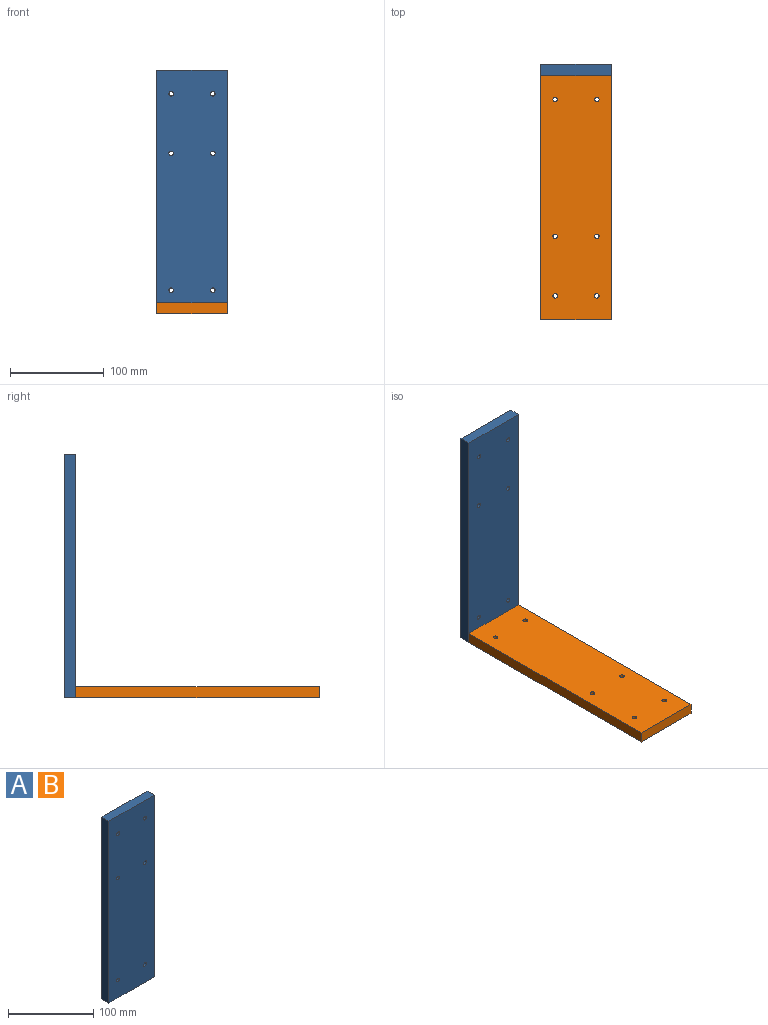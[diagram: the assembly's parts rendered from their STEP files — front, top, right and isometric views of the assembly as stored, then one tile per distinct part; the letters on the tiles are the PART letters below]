
ASSEMBLY  parts=2 mates=1
PART A: 12 faces, bbox 75x11.8x260.4 mm
  f0: plane 260.35x11.75mm, normal (1,0,0), area 3059.1mm2, adj f1,f3,f4,f5
  f1: plane 75x11.75mm, normal (0,0,1), area 881.2mm2, adj f0,f2,f4,f5
  f2: plane 260.35x11.75mm, normal (-1,0,0), area 3059.1mm2, adj f1,f3,f4,f5
  f3: plane 75x11.75mm, normal (0,0,-1), area 881.2mm2, adj f0,f2,f4,f5
  f4: plane 260.35x75mm, normal (0,-1,0), area 19419.4mm2, adj f0,f1,f2,f3,f6,f7,f8,f9
  f5: plane 260.35x75mm, normal (0,1,0), area 19419.4mm2, adj f0,f1,f2,f3,f6,f7,f8,f9
  f6: cylinder r=2.38mm len=11.75mm, axis (0,-1,0), area 175.8mm2, adj f4,f5
  f7: cylinder r=2.38mm len=11.75mm, axis (0,-1,0), area 175.8mm2, adj f4,f5
  f8: cylinder r=2.38mm len=11.75mm, axis (0,-1,0), area 175.8mm2, adj f4,f5
  f9: cylinder r=2.38mm len=11.75mm, axis (0,-1,0), area 175.8mm2, adj f4,f5
  f10: cylinder r=2.38mm len=11.75mm, axis (0,-1,0), area 175.8mm2, adj f4,f5
  f11: cylinder r=2.38mm len=11.75mm, axis (0,-1,0), area 175.8mm2, adj f4,f5
PART B: same geometry as A
PLACE A at identity fixed
PLACE B rot(axis=(0,-0.71,0.71),180deg) t=(0,-141.93,-130.18)mm
MATE fastened B.f3 <-> A.f4  axis (0,1,0) through (0,-11.75,-130.18)mm
